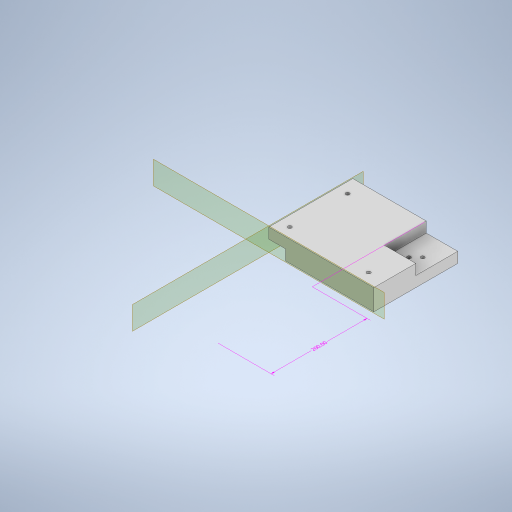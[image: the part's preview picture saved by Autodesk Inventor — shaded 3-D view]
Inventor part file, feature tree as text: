
AUTODESK INVENTOR PART (.ipt)
format: ipt  version: 2023 (Build 270158000, 158)  size: 427,008 bytes
history: native  units: mm
features: sketch x10, extrude x5, hole x5, other x3, plane x2, split x2
ambient origin geometry x8: Origin, YZ Plane, XZ Plane, XY Plane, X Axis, Y Axis, Z Axis, Center Point
bodies: Body1 (feature_tree)
feature tree (27):
  other  "Sólido1"
  other  "Anotaciones"
  extrude  "Extrusión1"  Depth=160.0mm
  extrude  "Extrusión2"  Depth=30.0mm
  hole  "Agujero1"  [1 undecoded]
  extrude  "Extrusión3"  Depth=11.75mm
  hole  "Agujero2"  [1 undecoded]
  hole  "Agujero3"  [1 undecoded]
  extrude  "Extrusión4"  TaperAngle=0.0deg  [1 undecoded]
  plane  "Plano de trabajo1"
  plane  "Plano de trabajo2"
  hole  "Agujero4"  [1 undecoded]
  hole  "Agujero5"  [1 undecoded]
  extrude  "Extrusión5"  Depth=70.0mm
  split  "Dividir1"
  split  "Dividir2"
  sketch  "Boceto1"  dims[d0=200.0mm d1=160.0mm]
  sketch  "Boceto2"  dims[d2=20.0mm d3=0.0mm d4=30.0mm]
  sketch  "Boceto3"  dims[d5=40.0mm d6=10.0mm d7=0.0mm]
  sketch  "Boceto4"  dims[d23=21.75mm d24=11.75mm]
  sketch  "Boceto5"  dims[d26=11.75mm]
  sketch  "Boceto6"  dims[d27=3.5mm d28=6.0mm d29=4.0mm d30=2.0mm d31=90.0deg d32=8.0mm d33=20.594885mm d34=30.0mm]
  sketch  "Boceto7"  dims[d35=10.0mm d36=30.0mm]
  sketch  "Boceto8"  dims[d37=40.0mm d38=0.0mm]
  sketch  "Boceto9"  dims[d39=10.0mm d40=10.0mm d41=40.0mm d42=0.0mm d43=6.5mm d44=6.5mm d45=3.5mm d46=3.5mm d47=11.749873mm d48=11.75mm d49=0.0mm]
  sketch  "Boceto10"  dims[d50=11.75mm d51=0.0mm d52=3.5mm d53=6.0mm d54=4.0mm d55=2.0mm d56=90.0deg d57=8.0mm d58=20.594885mm d59=7.0mm d60=7.0mm d61=7.0mm d62=39.0mm d63=46.0mm d64=59.0mm d65=46.0mm d66=39.0mm d67=59.0mm d68=52.0mm d69=70.0mm d70=22.0mm d71=42.0mm d72=3.5mm d73=3.5mm d74=3.5mm d75=3.5mm d76=3.5mm d77=6.0mm d78=4.0mm d79=2.0mm d80=90.0deg d81=8.0mm d82=20.594885mm d83=7.0mm d84=7.0mm d85=7.0mm d86=39.0mm d87=46.0mm d88=59.0mm d89=46.0mm d90=39.0mm d91=59.0mm d92=20.0mm d93=0.0mm d97=40.000127mm d98=10.0mm d99=30.0mm d100=10.0mm d101=5.0mm d102=5.0mm d103=5.0mm d104=5.0mm d105=45.0deg d106=45.0deg d107=10.0mm d108=10.0mm d109=30.0mm d110=5.0mm d111=5.0mm d112=5.0mm d113=5.0mm d114=10.0mm d115=30.0mm d116=5.0mm d117=5.0mm d118=5.0mm d119=5.0mm d120=10.0mm d121=3.5mm d122=6.0mm d123=4.0mm d124=2.0mm d125=90.0deg d126=8.0mm d127=20.594885mm d128=3.5mm d129=10.0mm d130=10.0mm d131=3.5mm d132=6.0mm d133=4.0mm d134=2.0mm d135=90.0deg d136=8.0mm d137=20.594885mm d138=32.0mm d139=32.0mm d140=10.0mm d141=0.0mm d142=17.37633mm d143=12.709242mm d144=6.683722mm d145=12.708891mm d146=5.220756mm d147=1.603663mm d148=2.153068mm d149=6.490327mm d94=6.100674mm d95=2.550465mm d96=200.0mm]
  other  "Cota lineal 1"
note: 6 required parameter values undecoded (feature->parameter linkage not recoverable at this tier; creation-order binding heuristic only, values carry confidence <= 0.55)
